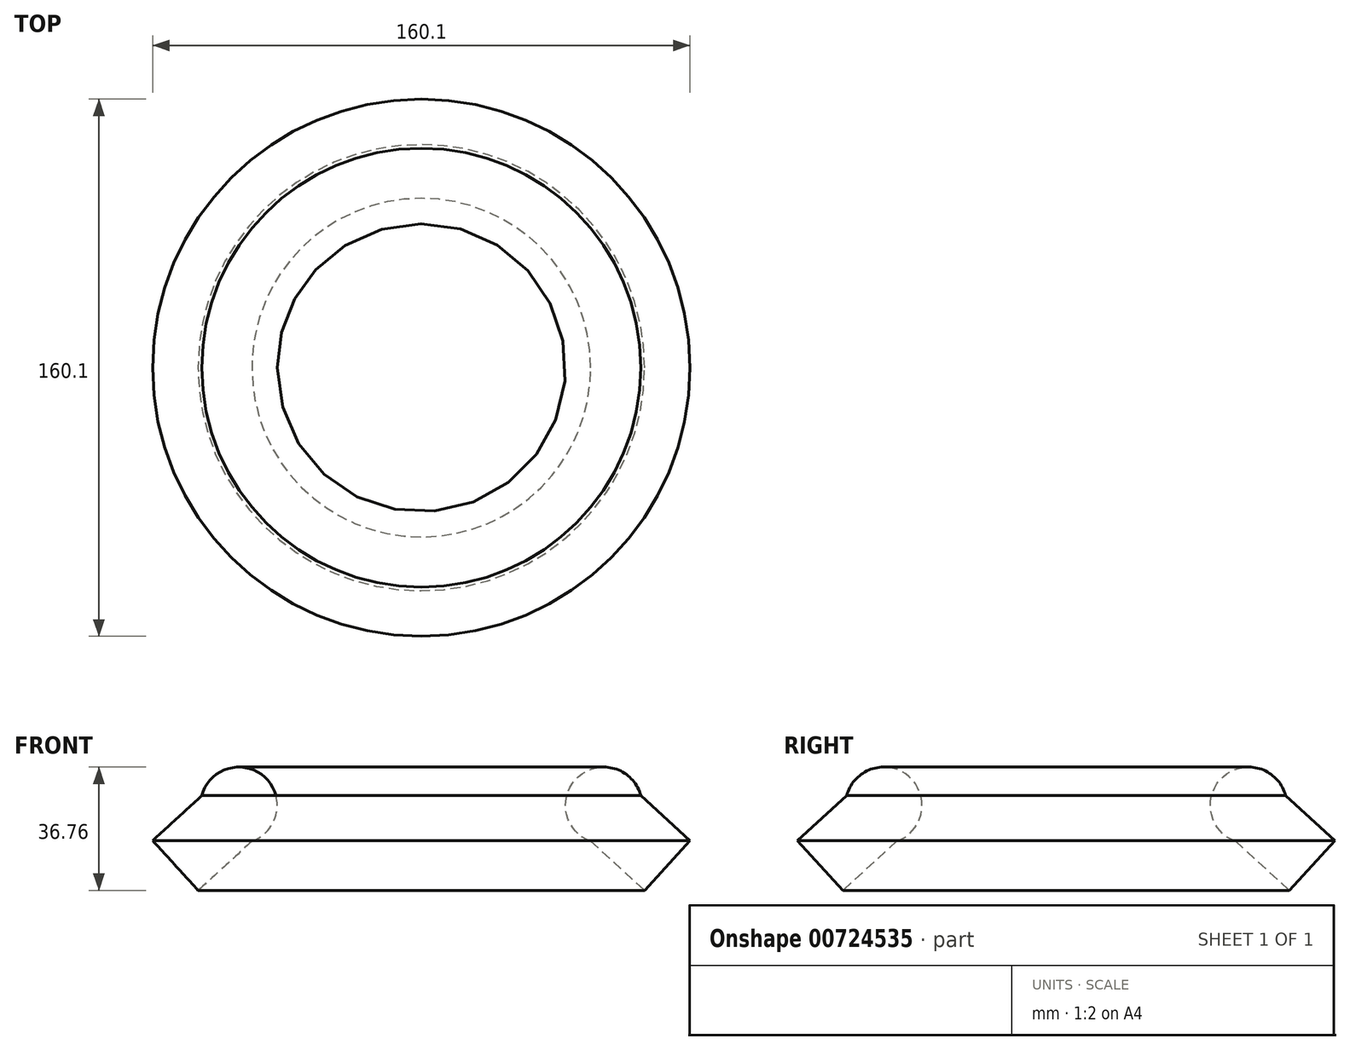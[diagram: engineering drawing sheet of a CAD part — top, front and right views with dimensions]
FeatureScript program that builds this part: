
annotation { "Feature Type Name" : "Feature", "Feature Type Description" : "" }
export const myFeature = defineFeature(function(context is Context, id is Id, definition is map)
    precondition{}
    {
        {
            var Q0;
            Q0=qCreatedBy(makeId("Front.planeOp"),FACE);
            var sketch = newSketch(context, id + "F0", { "sketchPlane" : qUnion([Q0])});
            skLineSegment(sketch, "E0", {"start": v(50.46, 6.2) * mm, "end": v(66.5, -8.43) * mm});
            skLineSegment(sketch, "E1", {"start": v(66.5, -8.43) * mm, "end": v(80.05, 6.43) * mm});
            skLineSegment(sketch, "E2", {"start": v(80.05, 6.43) * mm, "end": v(65.4, 19.8) * mm});
            skArc(sketch, "E3", {"start": v(65.4, 19.8) * mm, "mid": v(46.67, 25.35) * mm, "end": v(50.46, 6.2) * mm});
            skSolve(sketch);
        }
        {
            var Q0;
            Q0=qCreatedBy(makeId("Right.planeOp"),FACE);
            var sketch = newSketch(context, id + "F1", { "sketchPlane" : qUnion([Q0])});
            skLineSegment(sketch, "E4", {"start": v(0, 0) * mm, "end": v(0, -6.71) * mm});
            skLineSegment(sketch, "E5", {"start": v(0, -6.71) * mm, "end": v(0, 6.9) * mm});
            skSolve(sketch);
        }
        {
            var Q0;
            Q0=makeQuery(id+"F0.imprint","IMPRINT",FACE,{"disambiguationData":[TD([[makeQuery(id+"F0.imprint","IMPRINT",EDGE,{"derivedFrom":sQuery(id+"F0.wireOp",EDGE,"E0")}),1.0]])]});
            var Q1;
            Q1=sQuery(id+"F1.wireOp",EDGE,"E5");
            revolve(context, id + "F2", {"surfaceOperationType" : NewSurfaceOperationType.NEW, "entities" : qUnion([Q0]), "axis" : qUnion([Q1]), "revolveType" : RevolveType.FULL});
        }
    });
